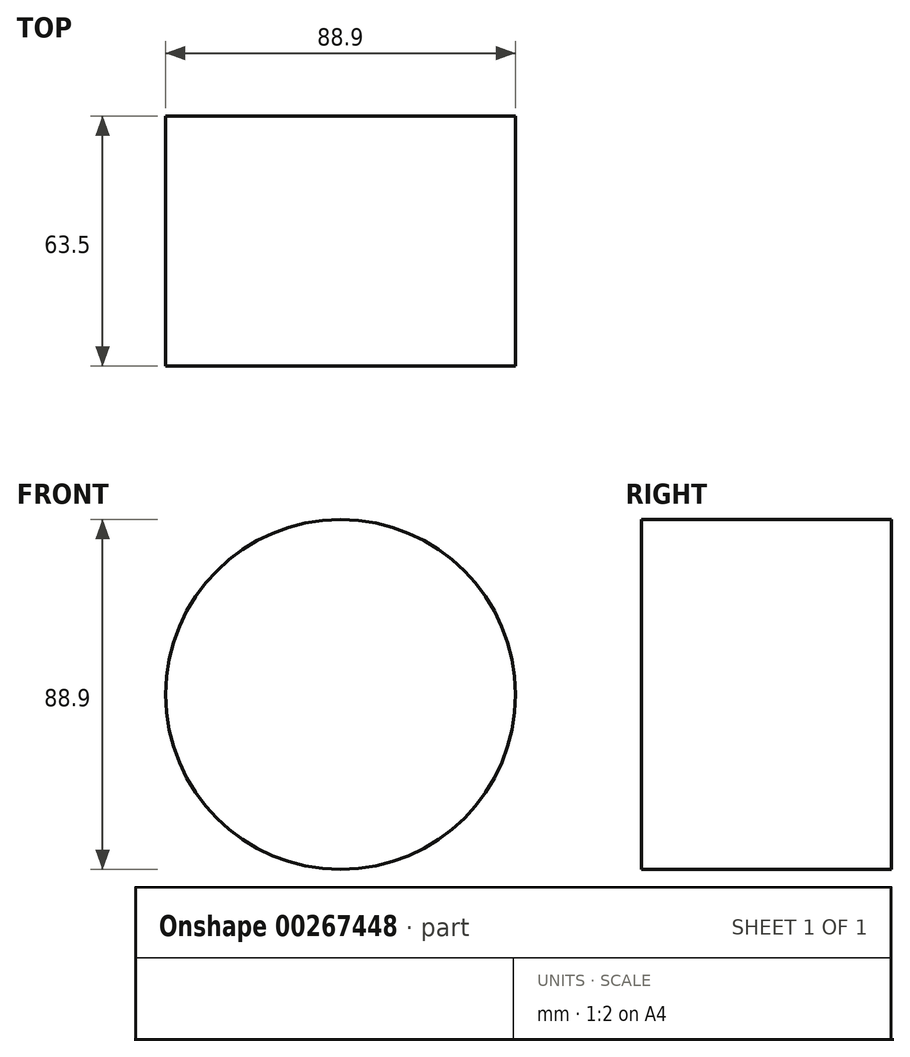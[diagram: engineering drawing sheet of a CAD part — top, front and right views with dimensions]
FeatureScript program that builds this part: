
annotation { "Feature Type Name" : "Feature", "Feature Type Description" : "" }
export const myFeature = defineFeature(function(context is Context, id is Id, definition is map)
    precondition{}
    {
        {
            var Q0;
            Q0=qCreatedBy(makeId("Front.planeOp"),FACE);
            var sketch = newSketch(context, id + "F0", { "sketchPlane" : qUnion([Q0])});
            skCircle(sketch, "E0", {"center": v(0, 0) * mm, "radius": 44.45 * mm});
            skSolve(sketch);
        }
        {
            var Q0;
            Q0 = qSketchRegion(id + "F0", true);
            extrude(context, id + "F1", {"entities" : qUnion([Q0]), "depth" : 63.5 * mm});
        }
    });
